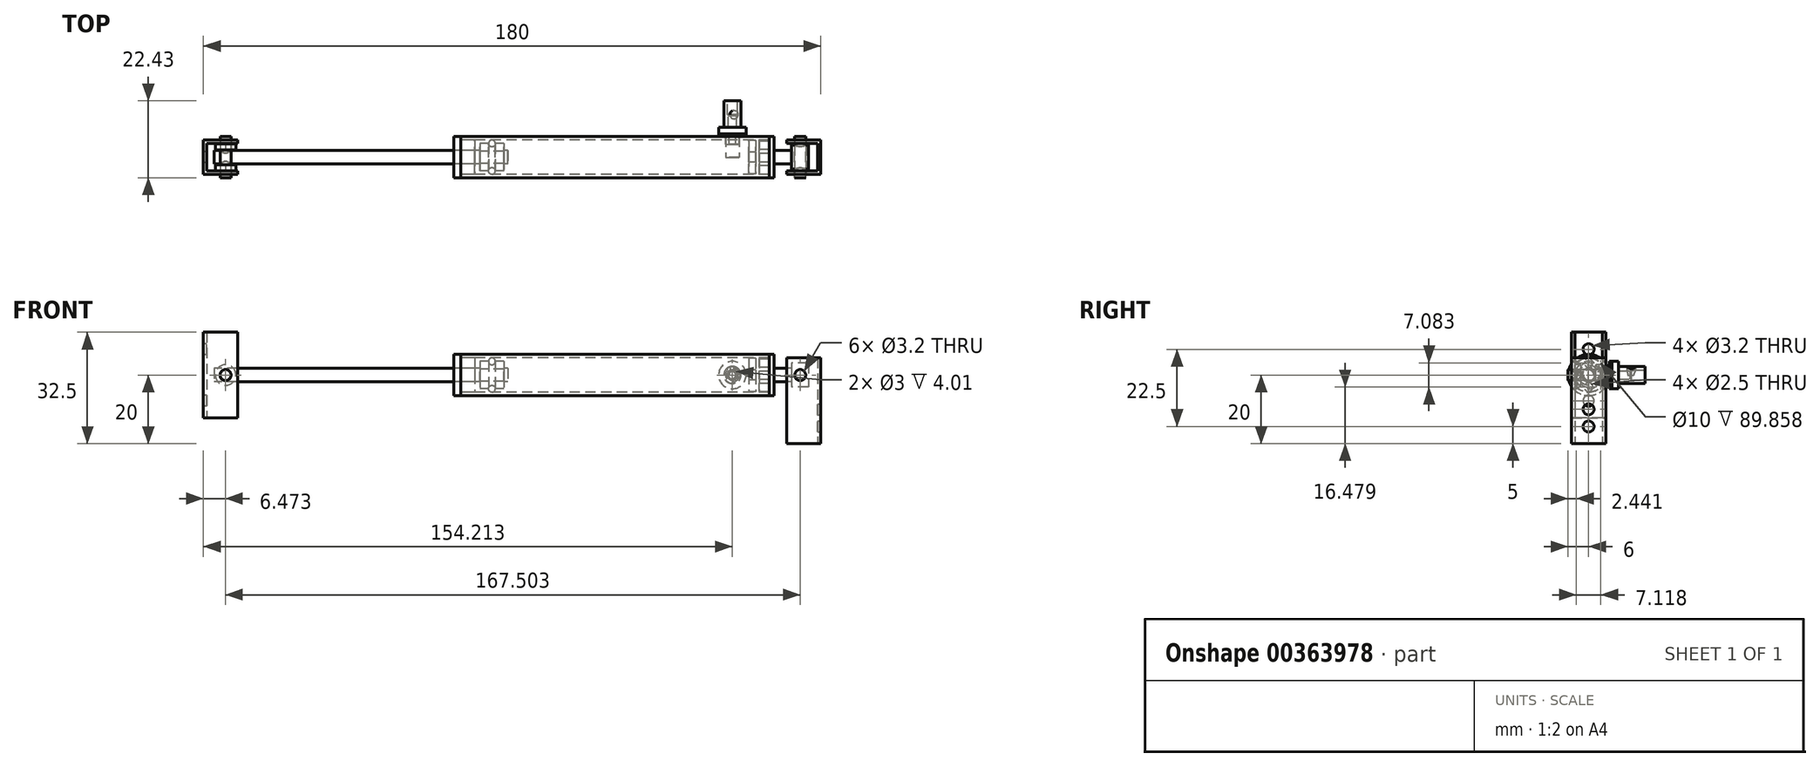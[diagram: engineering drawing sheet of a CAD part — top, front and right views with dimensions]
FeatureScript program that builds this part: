
annotation { "Feature Type Name" : "Feature", "Feature Type Description" : "" }
export const myFeature = defineFeature(function(context is Context, id is Id, definition is map)
    precondition{}
    {
        {
            var Q0;
            Q0=qCreatedBy(makeId("Top.planeOp"),FACE);
            var sketch = newSketch(context, id + "F0", { "sketchPlane" : qUnion([Q0])});
            skLineSegment(sketch, "E0", {"start": v(-90, -5) * mm, "end": v(-90, 5) * mm});
            skLineSegment(sketch, "E1", {"start": v(-90, 5) * mm, "end": v(-80, 5) * mm});
            skLineSegment(sketch, "E2", {"start": v(-80, 5) * mm, "end": v(-80, 4) * mm});
            skLineSegment(sketch, "E3", {"start": v(-80, 4) * mm, "end": v(-89, 4) * mm});
            skLineSegment(sketch, "E4", {"start": v(-89, 4) * mm, "end": v(-89, -4) * mm});
            skLineSegment(sketch, "E5", {"start": v(-89, -4) * mm, "end": v(-80, -4) * mm});
            skLineSegment(sketch, "E6", {"start": v(-80, -4) * mm, "end": v(-80, -5) * mm});
            skLineSegment(sketch, "E7", {"start": v(-80, -5) * mm, "end": v(-90, -5) * mm});
            skLineSegment(sketch, "E8.MirrorCS", {"start": v(80, 5) * mm, "end": v(80, 4) * mm});
            skLineSegment(sketch, "E9.MirrorCS", {"start": v(80, -4) * mm, "end": v(80, -5) * mm});
            skLineSegment(sketch, "E10.MirrorCS", {"start": v(80, 4) * mm, "end": v(89, 4) * mm});
            skLineSegment(sketch, "E11.MirrorCS", {"start": v(90, 5) * mm, "end": v(80, 5) * mm});
            skLineSegment(sketch, "E12.MirrorCS", {"start": v(90, -5) * mm, "end": v(90, 5) * mm});
            skLineSegment(sketch, "E13.MirrorCS", {"start": v(89, -4) * mm, "end": v(80, -4) * mm});
            skLineSegment(sketch, "E14.MirrorCS", {"start": v(80, -5) * mm, "end": v(90, -5) * mm});
            skLineSegment(sketch, "E15.MirrorCS", {"start": v(89, 4) * mm, "end": v(89, -4) * mm});
            skLineSegment(sketch, "E16.bottom", {"start": v(-80, 5) * mm, "end": v(-15, 5) * mm, "construction": true});
            skLineSegment(sketch, "E16.top", {"start": v(-80, -5) * mm, "end": v(-15, -5) * mm, "construction": true});
            skLineSegment(sketch, "E16.left", {"start": v(-80, 5) * mm, "end": v(-80, -5) * mm, "construction": true});
            skLineSegment(sketch, "E16.right", {"start": v(-15, 5) * mm, "end": v(-15, -5) * mm, "construction": true});
            skLineSegment(sketch, "E17.bottom", {"start": v(-86.5, 3.92) * mm, "end": v(-80.5, 3.92) * mm});
            skLineSegment(sketch, "E17.top", {"start": v(-86.5, 2.12) * mm, "end": v(-80.5, 2.12) * mm});
            skLineSegment(sketch, "E17.left", {"start": v(-86.5, 3.92) * mm, "end": v(-86.5, 2.12) * mm});
            skLineSegment(sketch, "E17.right", {"start": v(-80.5, 3.92) * mm, "end": v(-80.5, 2.12) * mm});
            skLineSegment(sketch, "E18", {"start": v(-83.5, 6.91) * mm, "end": v(-83.5, -7.28) * mm, "construction": true});
            skLineSegment(sketch, "E19", {"start": v(-83.5, -7.28) * mm, "end": v(-83.5, 6.04) * mm});
            skLineSegment(sketch, "E20.bottom", {"start": v(-85.1, 2.12) * mm, "end": v(-81.9, 2.12) * mm});
            skLineSegment(sketch, "E20.top", {"start": v(-85.1, 3.92) * mm, "end": v(-81.9, 3.92) * mm});
            skLineSegment(sketch, "E20.left", {"start": v(-85.1, 2.12) * mm, "end": v(-85.1, 3.92) * mm});
            skLineSegment(sketch, "E20.right", {"start": v(-81.9, 2.12) * mm, "end": v(-81.9, 3.92) * mm});
            skLineSegment(sketch, "E21.bottom", {"start": v(-86.5, -2.16) * mm, "end": v(-80.5, -2.16) * mm});
            skLineSegment(sketch, "E21.top", {"start": v(-86.5, -3.96) * mm, "end": v(-80.5, -3.96) * mm});
            skLineSegment(sketch, "E21.left", {"start": v(-86.5, -2.16) * mm, "end": v(-86.5, -3.96) * mm});
            skLineSegment(sketch, "E21.right", {"start": v(-80.5, -2.16) * mm, "end": v(-80.5, -3.96) * mm});
            skPoint(sketch, "E22.startSnap0", {"position": v(-83.5, -2.16) * mm});
            skLineSegment(sketch, "E23.bottom", {"start": v(-85.1, -3.96) * mm, "end": v(-81.9, -3.96) * mm});
            skLineSegment(sketch, "E23.top", {"start": v(-85.1, -2.16) * mm, "end": v(-81.9, -2.16) * mm});
            skLineSegment(sketch, "E23.left", {"start": v(-85.1, -3.96) * mm, "end": v(-85.1, -2.16) * mm});
            skLineSegment(sketch, "E23.right", {"start": v(-81.9, -3.96) * mm, "end": v(-81.9, -2.16) * mm});
            skSolve(sketch);
        }
        {
            var Q0;
            Q0=makeQuery(id+"F0.imprint","IMPRINT",FACE,{"disambiguationData":[TD([[makeQuery(id+"F0.imprint","IMPRINT",EDGE,{"derivedFrom":sQuery(id+"F0.wireOp",EDGE,"E0")}),-1.0]])]});
            var Q1;
            {var subQ5=sQuery(id+"F0.wireOp",EDGE,"E2");Q1=makeQuery(id+"F0.imprint","IMPRINT",FACE,{"disambiguationData":[TD([[makeQuery(id+"F0.imprint","IMPRINT",EDGE,{"derivedFrom":subQ5}),-1.0]])]});}
            var Q2;
            {var subQ0=sQuery(id+"F0.wireOp",EDGE,"E6");Q2=makeQuery(id+"F0.imprint","IMPRINT",FACE,{"disambiguationData":[TD([[makeQuery(id+"F0.imprint","IMPRINT",EDGE,{"derivedFrom":subQ0}),-1.0]])]});}
            extrude(context, id + "F1", {"entities" : qUnion([Q0, Q1, Q2]), "endBound" : BoundingType.SYMMETRIC, "depth" : 25 * mm});
        }
        {
            var Q0;
            Q0=makeQuery(id+"F0.imprint","IMPRINT",FACE,{"disambiguationData":[TD([[makeQuery(id+"F0.imprint","IMPRINT",EDGE,{"derivedFrom":sQuery(id+"F0.wireOp",EDGE,"E8.MirrorCS")}),1.0]])]});
            extrude(context, id + "F2", {"entities" : qUnion([Q0]), "depth" : 5 * mm, "hasSecondDirection" : true, "secondDirectionOppositeDirection" : true, "secondDirectionDepth" : 20 * mm});
        }
        {
            var Q0;
            Q0=qCreatedBy(makeId("Top.planeOp"),FACE);
            var sketch = newSketch(context, id + "F3", { "sketchPlane" : qUnion([Q0])});
            skLineSegment(sketch, "E24.bottom", {"start": v(-14.93, 6) * mm, "end": v(74.93, 6) * mm});
            skLineSegment(sketch, "E24.top", {"start": v(-14.93, -6) * mm, "end": v(74.93, -6) * mm});
            skLineSegment(sketch, "E24.left", {"start": v(-14.93, 6) * mm, "end": v(-14.93, -6) * mm});
            skLineSegment(sketch, "E24.right", {"start": v(74.93, 6) * mm, "end": v(74.93, -6) * mm});
            skLineSegment(sketch, "E25.top", {"start": v(-14.93, 5) * mm, "end": v(74.93, 5) * mm});
            skLineSegment(sketch, "E25.left", {"start": v(-14.93, 6) * mm, "end": v(-14.93, 5) * mm});
            skLineSegment(sketch, "E25.right", {"start": v(74.93, 6) * mm, "end": v(74.93, 5) * mm});
            skLineSegment(sketch, "E26.top", {"start": v(-14.93, -5) * mm, "end": v(74.93, -5) * mm});
            skLineSegment(sketch, "E26.left", {"start": v(-14.93, -6) * mm, "end": v(-14.93, -5) * mm});
            skLineSegment(sketch, "E26.right", {"start": v(74.93, -6) * mm, "end": v(74.93, -5) * mm});
            skLineSegment(sketch, "E27", {"start": v(-95.99, 0) * mm, "end": v(102.37, 0) * mm, "construction": true});
            skPoint(sketch, "E27.endSnap0", {"position": v(-14.93, 0) * mm});
            skSolve(sketch);
        }
        {
            var Q0;
            Q0=qCreatedBy(makeId("Top.planeOp"),FACE);
            var sketch = newSketch(context, id + "F4", { "sketchPlane" : qUnion([Q0])});
            skLineSegment(sketch, "E28.bottom", {"start": v(-108.9, 0) * mm, "end": v(81.37, 0) * mm, "construction": true});
            skLineSegment(sketch, "E28.top", {"start": v(-108.9, 0) * mm, "end": v(81.37, 0) * mm});
            skLineSegment(sketch, "E28.left", {"start": v(-108.9, 0) * mm, "end": v(-108.9, 0) * mm});
            skLineSegment(sketch, "E28.right", {"start": v(81.37, 0) * mm, "end": v(81.37, 0) * mm});
            skLineSegment(sketch, "E29.bottom", {"start": v(-86.9, 2) * mm, "end": v(-1.24, 2) * mm});
            skLineSegment(sketch, "E29.top", {"start": v(-86.9, -2) * mm, "end": v(-1.24, -2) * mm});
            skLineSegment(sketch, "E29.left", {"start": v(-86.9, 2) * mm, "end": v(-86.9, -2) * mm});
            skLineSegment(sketch, "E29.right", {"start": v(-1.24, 2) * mm, "end": v(-1.24, -2) * mm});
            skSolve(sketch);
        }
        {
            var Q0;
            Q0=makeQuery(id+"F3.imprint","IMPRINT",FACE,{"disambiguationData":[TD([[makeQuery(id+"F3.imprint","IMPRINT",EDGE,{"derivedFrom":sQuery(id+"F3.wireOp",EDGE,"E24.bottom")}),-1.0]])]});
            var Q1;
            Q1=sQuery(id+"F3.wireOp",EDGE,"E27");
            revolve(context, id + "F5", {"entities" : qUnion([Q0]), "axis" : qUnion([Q1]), "revolveType" : RevolveType.FULL});
        }
        {
            var Q0;
            {var subQ5=sQuery(id+"F4.wireOp",EDGE,"E29.bottom");Q0=makeQuery(id+"F4.imprint","IMPRINT",FACE,{"disambiguationData":[TD([[makeQuery(id+"F4.imprint","IMPRINT",EDGE,{"derivedFrom":subQ5}),-1.0]])]});}
            var Q1;
            Q1=sQuery(id+"F4.wireOp",EDGE,"E28.top");
            revolve(context, id + "F6", {"entities" : qUnion([Q0]), "axis" : qUnion([Q1]), "revolveType" : RevolveType.FULL});
        }
        {
            var Q0;
            Q0=qCreatedBy(makeId("Top.planeOp"),FACE);
            var sketch = newSketch(context, id + "F7", { "sketchPlane" : qUnion([Q0])});
            skLineSegment(sketch, "E30.bottom", {"start": v(-9.38, 4) * mm, "end": v(-6.88, 4) * mm});
            skLineSegment(sketch, "E30.top", {"start": v(-9.38, -4) * mm, "end": v(-2.38, -4) * mm});
            skLineSegment(sketch, "E30.left", {"start": v(-9.38, 4) * mm, "end": v(-9.38, -4) * mm});
            skLineSegment(sketch, "E30.right", {"start": v(-2.38, 4) * mm, "end": v(-2.38, -4) * mm});
            skCircle(sketch, "E31", {"center": v(-5.88, 4) * mm, "radius": 1 * mm});
            skLineSegment(sketch, "E32.top", {"start": v(-9.38, 1.77) * mm, "end": v(-2.38, 1.77) * mm});
            skLineSegment(sketch, "E32.left", {"start": v(-9.38, 4) * mm, "end": v(-9.38, 1.77) * mm});
            skLineSegment(sketch, "E32.right", {"start": v(-2.38, 4) * mm, "end": v(-2.38, 1.77) * mm});
            skLineSegment(sketch, "E33", {"start": v(-4.88, 4) * mm, "end": v(-2.38, 4) * mm});
            skLineSegment(sketch, "E34", {"start": v(-7.97, 0) * mm, "end": v(19.48, 0) * mm, "construction": true});
            skLineSegment(sketch, "E35.bottom", {"start": v(-5.83, 14.1) * mm, "end": v(54.17, 14.1) * mm, "construction": true});
            skLineSegment(sketch, "E35.top", {"start": v(-5.83, -9.63) * mm, "end": v(54.17, -9.63) * mm, "construction": true});
            skLineSegment(sketch, "E35.left", {"start": v(-5.83, 14.1) * mm, "end": v(-5.83, -9.63) * mm, "construction": true});
            skLineSegment(sketch, "E35.right", {"start": v(54.17, 14.1) * mm, "end": v(54.17, -9.63) * mm, "construction": true});
            skSolve(sketch);
        }
        {
            var Q0;
            {var subQ0=sQuery(id+"F7.wireOp",EDGE,"E31");var subQ1=makeQuery(id+"F7.imprint","INTERSECT",VERTEX,{"derivedFrom":[subQ0,sQuery(id+"F7.wireOp",EDGE,"E30.bottom")]});Q0=makeQuery(id+"F7.imprint","IMPRINT",FACE,{"disambiguationData":[TD([[makeQuery(id+"F7.imprint","IMPRINT",EDGE,{"disambiguationData":[TD([[subQ1,1.0]])],"derivedFrom":subQ0}),1.0]])]});}
            var Q1;
            Q1=sQuery(id+"F7.wireOp",EDGE,"E34");
            revolve(context, id + "F8", {"entities" : qUnion([Q0]), "axis" : qUnion([Q1]), "revolveType" : RevolveType.FULL});
        }
        {
            var Q0;
            {var subQ0=sQuery(id+"F7.wireOp",EDGE,"E30.bottom");Q0=makeQuery(id+"F7.imprint","IMPRINT",FACE,{"disambiguationData":[TD([[makeQuery(id+"F7.imprint","IMPRINT",EDGE,{"derivedFrom":subQ0}),-1.0]])]});}
            var Q1;
            Q1=sQuery(id+"F7.wireOp",EDGE,"E34");
            revolve(context, id + "F9", {"operationType" : NewBodyOperationType.REMOVE, "entities" : qUnion([Q0]), "axis" : qUnion([Q1]), "revolveType" : RevolveType.FULL});
        }
        {
            var Q0;
            {var subQ0=sQuery(id+"F7.wireOp",EDGE,"E30.bottom");Q0=makeQuery(id+"F7.imprint","IMPRINT",FACE,{"disambiguationData":[TD([[makeQuery(id+"F7.imprint","IMPRINT",EDGE,{"derivedFrom":subQ0}),-1.0]])]});}
            var Q1;
            Q1=sQuery(id+"F7.wireOp",EDGE,"E34");
            revolve(context, id + "F10", {"entities" : qUnion([Q0]), "axis" : qUnion([Q1]), "revolveType" : RevolveType.FULL});
        }
        {
            var Q0;
            {var subQ0=sQuery(id+"F7.wireOp",EDGE,"E31");var subQ1=makeQuery(id+"F7.imprint","INTERSECT",VERTEX,{"derivedFrom":[subQ0,sQuery(id+"F7.wireOp",EDGE,"E30.bottom")]});Q0=makeQuery(id+"F7.imprint","IMPRINT",FACE,{"disambiguationData":[TD([[makeQuery(id+"F7.imprint","IMPRINT",EDGE,{"disambiguationData":[TD([[subQ1,1.0]])],"derivedFrom":subQ0}),1.0]])]});}
            var Q1;
            Q1=sQuery(id+"F7.wireOp",EDGE,"E31");
            var Q2;
            Q2=sQuery(id+"F7.wireOp",EDGE,"E34");
            revolve(context, id + "F11", {"entities" : qUnion([Q0]), "surfaceEntities" : qUnion([Q1]), "axis" : qUnion([Q2]), "revolveType" : RevolveType.FULL});
        }
        {
            var Q0;
            Q0=makeQuery(id+"F8.opRevolve","SWEPT_BODY",BODY,{"disambiguationData":[OSD([sQuery(id+"F7.wireOp",EDGE,"E31")])]});
            deleteBodies(context, id + "F12", {"entities" : qUnion([Q0])});
        }
        {
            var Q0;
            Q0=qCreatedBy(makeId("Top.planeOp"),FACE);
            var sketch = newSketch(context, id + "F13", { "sketchPlane" : qUnion([Q0])});
            skLineSegment(sketch, "E36.bottom", {"start": v(-14.94, 6) * mm, "end": v(-16.94, 6) * mm});
            skLineSegment(sketch, "E36.top", {"start": v(-14.94, -6) * mm, "end": v(-16.94, -6) * mm});
            skLineSegment(sketch, "E36.left", {"start": v(-14.94, 6) * mm, "end": v(-14.94, -6) * mm});
            skLineSegment(sketch, "E36.right", {"start": v(-16.94, 6) * mm, "end": v(-16.94, -6) * mm});
            skLineSegment(sketch, "E37.bottom", {"start": v(-14.94, 5) * mm, "end": v(-10.94, 5) * mm});
            skLineSegment(sketch, "E37.top", {"start": v(-14.94, -5) * mm, "end": v(-10.94, -5) * mm});
            skLineSegment(sketch, "E37.left", {"start": v(-14.94, 5) * mm, "end": v(-14.94, -5) * mm});
            skLineSegment(sketch, "E37.right", {"start": v(-10.94, 5) * mm, "end": v(-10.94, -5) * mm});
            skLineSegment(sketch, "E38", {"start": v(-16.94, 2) * mm, "end": v(-10.94, 2) * mm});
            skLineSegment(sketch, "E39", {"start": v(-16.94, -1.98) * mm, "end": v(-10.94, -1.98) * mm});
            skSolve(sketch);
        }
        {
            var Q0;
            {var subQ6=sQuery(id+"F13.wireOp",EDGE,"E36.bottom");Q0=makeQuery(id+"F13.imprint","IMPRINT",FACE,{"disambiguationData":[TD([[makeQuery(id+"F13.imprint","IMPRINT",EDGE,{"derivedFrom":subQ6}),1.0]])]});}
            var Q1;
            {var subQ0=sQuery(id+"F13.wireOp",EDGE,"E37.bottom");Q1=makeQuery(id+"F13.imprint","IMPRINT",FACE,{"disambiguationData":[TD([[makeQuery(id+"F13.imprint","IMPRINT",EDGE,{"derivedFrom":subQ0}),-1.0]])]});}
            var Q2;
            Q2=sQuery(id+"F4.wireOp",EDGE,"E28.top");
            revolve(context, id + "F14", {"entities" : qUnion([Q0, Q1]), "axis" : qUnion([Q2]), "revolveType" : RevolveType.FULL});
        }
        {
            var Q0;
            Q0=qCreatedBy(makeId("Top.planeOp"),FACE);
            var sketch = newSketch(context, id + "F15", { "sketchPlane" : qUnion([Q0])});
            skLineSegment(sketch, "E40.bottom", {"start": v(74.9, 6) * mm, "end": v(76.3, 6) * mm});
            skLineSegment(sketch, "E40.top", {"start": v(74.9, -6) * mm, "end": v(76.3, -6) * mm});
            skLineSegment(sketch, "E40.left", {"start": v(74.9, 6) * mm, "end": v(74.9, -6) * mm});
            skLineSegment(sketch, "E40.right", {"start": v(76.3, 6) * mm, "end": v(76.3, -6) * mm});
            skLineSegment(sketch, "E41.bottom", {"start": v(74.9, 5) * mm, "end": v(72.07, 5) * mm});
            skLineSegment(sketch, "E41.top", {"start": v(74.9, -5) * mm, "end": v(72.07, -5) * mm});
            skLineSegment(sketch, "E41.left", {"start": v(74.9, 5) * mm, "end": v(74.9, -5) * mm});
            skLineSegment(sketch, "E41.right", {"start": v(72.07, 5) * mm, "end": v(72.07, -5) * mm});
            skLineSegment(sketch, "E42.bottom", {"start": v(76.3, 2) * mm, "end": v(81.44, 2) * mm});
            skLineSegment(sketch, "E42.top", {"start": v(76.3, -2) * mm, "end": v(81.44, -2) * mm});
            skLineSegment(sketch, "E42.left", {"start": v(76.3, 2) * mm, "end": v(76.3, -2) * mm});
            skLineSegment(sketch, "E42.right", {"start": v(81.44, 2) * mm, "end": v(81.44, -2) * mm});
            skLineSegment(sketch, "E43.bottom", {"start": v(81.44, 3.5) * mm, "end": v(86.39, 3.5) * mm});
            skLineSegment(sketch, "E43.top", {"start": v(81.44, -3.5) * mm, "end": v(86.39, -3.5) * mm});
            skLineSegment(sketch, "E43.left", {"start": v(81.44, 3.5) * mm, "end": v(81.44, -3.5) * mm});
            skLineSegment(sketch, "E43.right", {"start": v(86.39, 3.5) * mm, "end": v(86.39, -3.5) * mm});
            skLineSegment(sketch, "E44", {"start": v(66.23, 0) * mm, "end": v(91.9, 0) * mm, "construction": true});
            skPoint(sketch, "E44.endSnap0", {"position": v(81.44, 0) * mm});
            skLineSegment(sketch, "E45", {"start": v(72.07, 0) * mm, "end": v(86.39, 0) * mm});
            skLineSegment(sketch, "E46.bottom", {"start": v(69, 4.9) * mm, "end": v(71, 4.9) * mm});
            skLineSegment(sketch, "E46.top", {"start": v(69, 1.5) * mm, "end": v(71, 1.5) * mm});
            skLineSegment(sketch, "E46.left", {"start": v(69, 4.9) * mm, "end": v(69, 1.5) * mm});
            skLineSegment(sketch, "E46.right", {"start": v(71, 4.9) * mm, "end": v(71, 1.5) * mm});
            skSolve(sketch);
        }
        {
            var Q0;
            Q0=makeQuery(id+"F15.imprint","IMPRINT",FACE,{"disambiguationData":[TD([[makeQuery(id+"F15.imprint","IMPRINT",EDGE,{"derivedFrom":sQuery(id+"F15.wireOp",EDGE,"E41.bottom")}),1.0]])]});
            var Q1;
            {var subQ3=sQuery(id+"F15.wireOp",EDGE,"E40.bottom");Q1=makeQuery(id+"F15.imprint","IMPRINT",FACE,{"disambiguationData":[TD([[makeQuery(id+"F15.imprint","IMPRINT",EDGE,{"derivedFrom":subQ3}),-1.0]])]});}
            var Q2;
            {var subQ0=sQuery(id+"F15.wireOp",EDGE,"E42.bottom");Q2=makeQuery(id+"F15.imprint","IMPRINT",FACE,{"disambiguationData":[TD([[makeQuery(id+"F15.imprint","IMPRINT",EDGE,{"derivedFrom":subQ0}),-1.0]])]});}
            var Q3;
            {var subQ3=sQuery(id+"F15.wireOp",EDGE,"E43.bottom");Q3=makeQuery(id+"F15.imprint","IMPRINT",FACE,{"disambiguationData":[TD([[makeQuery(id+"F15.imprint","IMPRINT",EDGE,{"derivedFrom":subQ3}),-1.0]])]});}
            var Q4;
            Q4=sQuery(id+"F4.wireOp",EDGE,"E28.top");
            revolve(context, id + "F16", {"entities" : qUnion([Q0, Q1, Q2, Q3]), "axis" : qUnion([Q4]), "revolveType" : RevolveType.FULL});
        }
        {
            var Q0;
            Q0=makeQuery(id+"F16.opRevolve","SWEPT_FACE",FACE,{"disambiguationData":[OSD([sQuery(id+"F15.wireOp",EDGE,"E40.right")])]});
            var sketch = newSketch(context, id + "F17", { "sketchPlane" : qUnion([Q0])});
            skCircle(sketch, "E47", {"center": v(-0.02, 3.56) * mm, "radius": 1.25 * mm});
            skCircle(sketch, "E48", {"center": v(0, 0) * mm, "radius": 3.56 * mm, "construction": true});
            skCircle(sketch, "E49", {"center": v(3.56, 0) * mm, "radius": 1.25 * mm});
            skCircle(sketch, "E50", {"center": v(-0.02, -3.52) * mm, "radius": 1.25 * mm});
            skCircle(sketch, "E51", {"center": v(-3.56, 0) * mm, "radius": 1.25 * mm});
            skSolve(sketch);
        }
        {
            var Q0;
            Q0=makeQuery(id+"F17.imprint","IMPRINT",FACE,{"disambiguationData":[TD([[makeQuery(id+"F17.imprint","IMPRINT",EDGE,{"derivedFrom":sQuery(id+"F17.wireOp",EDGE,"E47")}),1.0]])]});
            var Q1;
            Q1=makeQuery(id+"F17.imprint","IMPRINT",FACE,{"disambiguationData":[TD([[makeQuery(id+"F17.imprint","IMPRINT",EDGE,{"derivedFrom":sQuery(id+"F17.wireOp",EDGE,"E51")}),1.0]])]});
            var Q2;
            Q2=makeQuery(id+"F17.imprint","IMPRINT",FACE,{"disambiguationData":[TD([[makeQuery(id+"F17.imprint","IMPRINT",EDGE,{"derivedFrom":sQuery(id+"F17.wireOp",EDGE,"E50")}),1.0]])]});
            var Q3;
            Q3=makeQuery(id+"F17.imprint","IMPRINT",FACE,{"disambiguationData":[TD([[makeQuery(id+"F17.imprint","IMPRINT",EDGE,{"derivedFrom":sQuery(id+"F17.wireOp",EDGE,"E49")}),1.0]])]});
            extrude(context, id + "F18", {"entities" : qUnion([Q0, Q1, Q2, Q3]), "operationType" : NewBodyOperationType.REMOVE, "endBound" : BoundingType.UP_TO_NEXT, "oppositeDirection" : true, "depth" : 25 * mm});
        }
        {
            var Q0;
            Q0=makeQuery(id+"F15.imprint","IMPRINT",FACE,{"disambiguationData":[TD([[makeQuery(id+"F15.imprint","IMPRINT",EDGE,{"derivedFrom":sQuery(id+"F15.wireOp",EDGE,"E46.bottom")}),-1.0]])]});
            var Q1;
            Q1=sQuery(id+"F4.wireOp",EDGE,"E28.top");
            revolve(context, id + "F19", {"entities" : qUnion([Q0]), "axis" : qUnion([Q1]), "revolveType" : RevolveType.FULL});
        }
        {
            var Q0;
            {var subQ0=sQuery(id+"F0.wireOp",EDGE,"E17.right");Q0=makeQuery(id+"F0.imprint","IMPRINT",FACE,{"disambiguationData":[TD([[makeQuery(id+"F0.imprint","IMPRINT",EDGE,{"derivedFrom":subQ0}),-1.0]])]});}
            var Q1;
            {var subQ0=sQuery(id+"F0.wireOp",EDGE,"E21.right");Q1=makeQuery(id+"F0.imprint","IMPRINT",FACE,{"disambiguationData":[TD([[makeQuery(id+"F0.imprint","IMPRINT",EDGE,{"derivedFrom":subQ0}),-1.0]])]});}
            var Q2;
            Q2=sQuery(id+"F0.wireOp",EDGE,"E19");
            revolve(context, id + "F20", {"operationType" : NewBodyOperationType.ADD, "entities" : qUnion([Q0, Q1]), "axis" : qUnion([Q2]), "revolveType" : RevolveType.FULL});
        }
        {
            var Q0;
            Q0=makeQuery(id+"F1.opExtrude","SWEPT_FACE",FACE,{"disambiguationData":[OSD([sQuery(id+"F0.wireOp",EDGE,"E7")])]});
            var sketch = newSketch(context, id + "F21", { "sketchPlane" : qUnion([Q0])});
            skCircle(sketch, "E52", {"center": v(-83.53, 0) * mm, "radius": 1.6 * mm});
            skSolve(sketch);
        }
        {
            var Q0;
            Q0=makeQuery(id+"F21.imprint","IMPRINT",FACE,{"disambiguationData":[TD([[makeQuery(id+"F21.imprint","IMPRINT",EDGE,{"derivedFrom":sQuery(id+"F21.wireOp",EDGE,"E52")}),1.0]])]});
            extrude(context, id + "F22", {"entities" : qUnion([Q0]), "oppositeDirection" : true, "depth" : 12 * mm, "hasSecondDirection" : true, "secondDirectionOppositeDirection" : true, "secondDirectionDepth" : -2 * mm});
        }
        {
            var Q0;
            Q0=qCreatedBy(makeId("Top.planeOp"),FACE);
            var sketch = newSketch(context, id + "F23", { "sketchPlane" : qUnion([Q0])});
            skLineSegment(sketch, "E53.bottom", {"start": v(60.21, 6.76) * mm, "end": v(68.21, 6.76) * mm});
            skLineSegment(sketch, "E53.top", {"start": v(60.21, 8.76) * mm, "end": v(68.21, 8.76) * mm});
            skLineSegment(sketch, "E53.left", {"start": v(60.21, 6.76) * mm, "end": v(60.21, 8.76) * mm});
            skLineSegment(sketch, "E53.right", {"start": v(68.21, 6.76) * mm, "end": v(68.21, 8.76) * mm});
            skLineSegment(sketch, "E54.bottom", {"start": v(63.21, 8.76) * mm, "end": v(65.21, 8.76) * mm});
            skLineSegment(sketch, "E54.top", {"start": v(63.21, 6.76) * mm, "end": v(65.21, 6.76) * mm});
            skLineSegment(sketch, "E54.left", {"start": v(63.21, 8.76) * mm, "end": v(63.21, 3.79) * mm});
            skLineSegment(sketch, "E54.right", {"start": v(65.21, 8.76) * mm, "end": v(65.21, 3.79) * mm});
            skLineSegment(sketch, "E55", {"start": v(64.21, 25.99) * mm, "end": v(64.21, 1.15) * mm, "construction": true});
            skLineSegment(sketch, "E56.bottom", {"start": v(62.21, 6.76) * mm, "end": v(66.21, 6.76) * mm});
            skLineSegment(sketch, "E56.top", {"start": v(62.21, 3.79) * mm, "end": v(66.21, 3.79) * mm});
            skLineSegment(sketch, "E56.left", {"start": v(62.21, 6.76) * mm, "end": v(62.21, 3.79) * mm});
            skLineSegment(sketch, "E56.right", {"start": v(66.21, 6.76) * mm, "end": v(66.21, 3.79) * mm});
            skLineSegment(sketch, "E57.bottom", {"start": v(60.21, 6.67) * mm, "end": v(61.81, 6.67) * mm});
            skLineSegment(sketch, "E57.top", {"start": v(60.21, 6.08) * mm, "end": v(61.81, 6.08) * mm});
            skLineSegment(sketch, "E57.left", {"start": v(60.21, 6.67) * mm, "end": v(60.21, 6.08) * mm});
            skLineSegment(sketch, "E57.right", {"start": v(61.81, 6.67) * mm, "end": v(61.81, 6.08) * mm});
            skLineSegment(sketch, "E58.bottom", {"start": v(61.71, 8.76) * mm, "end": v(66.71, 8.76) * mm});
            skLineSegment(sketch, "E58.top", {"start": v(61.71, 16.43) * mm, "end": v(66.71, 16.43) * mm});
            skLineSegment(sketch, "E58.left", {"start": v(61.71, 8.76) * mm, "end": v(61.71, 16.43) * mm});
            skLineSegment(sketch, "E58.right", {"start": v(66.71, 8.76) * mm, "end": v(66.71, 16.43) * mm});
            skLineSegment(sketch, "E59.bottom", {"start": v(63.01, 8.76) * mm, "end": v(65.41, 8.76) * mm});
            skLineSegment(sketch, "E59.top", {"start": v(63.01, 16.43) * mm, "end": v(65.41, 16.43) * mm});
            skLineSegment(sketch, "E59.left", {"start": v(63.01, 8.76) * mm, "end": v(63.01, 16.43) * mm});
            skLineSegment(sketch, "E59.right", {"start": v(65.41, 8.76) * mm, "end": v(65.41, 16.43) * mm});
            skLineSegment(sketch, "E60.bottom", {"start": v(61.46, 20.92) * mm, "end": v(66.96, 20.92) * mm});
            skLineSegment(sketch, "E60.top", {"start": v(61.46, 18.42) * mm, "end": v(66.96, 18.42) * mm});
            skLineSegment(sketch, "E60.left", {"start": v(61.46, 20.92) * mm, "end": v(61.46, 18.42) * mm});
            skLineSegment(sketch, "E60.right", {"start": v(66.96, 20.92) * mm, "end": v(66.96, 18.42) * mm});
            skLineSegment(sketch, "E61.bottom", {"start": v(62.71, 18.42) * mm, "end": v(65.71, 18.42) * mm});
            skLineSegment(sketch, "E61.top", {"start": v(62.71, 12.42) * mm, "end": v(65.71, 12.42) * mm});
            skLineSegment(sketch, "E61.left", {"start": v(62.71, 18.42) * mm, "end": v(62.71, 12.42) * mm});
            skLineSegment(sketch, "E61.right", {"start": v(65.71, 18.42) * mm, "end": v(65.71, 12.42) * mm});
            skCircle(sketch, "E62", {"center": v(64.21, 12.44) * mm, "radius": 1.25 * mm});
            skLineSegment(sketch, "E63.bottom", {"start": v(61.46, 20.92) * mm, "end": v(64.21, 20.92) * mm});
            skLineSegment(sketch, "E63.top", {"start": v(61.46, 18.42) * mm, "end": v(64.21, 18.42) * mm});
            skLineSegment(sketch, "E63.right", {"start": v(64.21, 20.92) * mm, "end": v(64.21, 18.42) * mm});
            skLineSegment(sketch, "E64.bottom", {"start": v(62.71, 18.42) * mm, "end": v(64.21, 18.42) * mm});
            skLineSegment(sketch, "E64.top", {"start": v(62.71, 12.42) * mm, "end": v(64.21, 12.42) * mm});
            skLineSegment(sketch, "E64.right", {"start": v(64.21, 18.42) * mm, "end": v(64.21, 12.42) * mm});
            skSolve(sketch);
        }
        {
            var Q0;
            {var subQ0=sQuery(id+"F23.wireOp",EDGE,"E53.left");Q0=makeQuery(id+"F23.imprint","IMPRINT",FACE,{"disambiguationData":[TD([[makeQuery(id+"F23.imprint","IMPRINT",EDGE,{"derivedFrom":subQ0}),-1.0]])]});}
            var Q1;
            {var subQ5=sQuery(id+"F23.wireOp",EDGE,"E56.left");Q1=makeQuery(id+"F23.imprint","IMPRINT",FACE,{"disambiguationData":[TD([[makeQuery(id+"F23.imprint","IMPRINT",EDGE,{"derivedFrom":subQ5}),1.0]])]});}
            var Q2;
            {var subQ0=sQuery(id+"F23.wireOp",EDGE,"E58.left");Q2=makeQuery(id+"F23.imprint","IMPRINT",FACE,{"disambiguationData":[TD([[makeQuery(id+"F23.imprint","IMPRINT",EDGE,{"derivedFrom":subQ0}),-1.0]])]});}
            var Q3;
            Q3=sQuery(id+"F23.wireOp",EDGE,"E55");
            revolve(context, id + "F24", {"entities" : qUnion([Q0, Q1, Q2]), "axis" : qUnion([Q3]), "revolveType" : RevolveType.FULL});
        }
        {
            var Q0;
            Q0=makeQuery(id+"F23.imprint","IMPRINT",FACE,{"disambiguationData":[TD([[makeQuery(id+"F23.imprint","IMPRINT",EDGE,{"derivedFrom":sQuery(id+"F23.wireOp",EDGE,"E57.bottom")}),-1.0]])]});
            var Q1;
            Q1=sQuery(id+"F23.wireOp",EDGE,"E55");
            revolve(context, id + "F25", {"entities" : qUnion([Q0]), "axis" : qUnion([Q1]), "revolveType" : RevolveType.FULL});
        }
        {
            var Q0;
            Q0=qCreatedBy(makeId("Top.planeOp"),FACE);
            var sketch = newSketch(context, id + "F26", { "sketchPlane" : qUnion([Q0])});
            skCircle(sketch, "E65", {"center": v(64.71, 12.42) * mm, "radius": 1.23 * mm});
            skSolve(sketch);
        }
        {
            var Q0;
            Q0 = qSketchRegion(id + "F26", true);
            extrude(context, id + "F27", {"entities" : qUnion([Q0]), "operationType" : NewBodyOperationType.REMOVE, "endBound" : BoundingType.THROUGH_ALL, "depth" : 25 * mm});
        }
        {
            var Q0;
            Q0=makeQuery(id+"F23.imprint","IMPRINT",FACE,{"disambiguationData":[TD([[makeQuery(id+"F23.imprint","IMPRINT",EDGE,{"derivedFrom":sQuery(id+"F23.wireOp",EDGE,"E63.bottom")}),-1.0]])]});
            var Q1;
            {var subQ1=sQuery(id+"F23.wireOp",EDGE,"E64.bottom");Q1=makeQuery(id+"F23.imprint","IMPRINT",FACE,{"disambiguationData":[TD([[makeQuery(id+"F23.imprint","IMPRINT",EDGE,{"derivedFrom":subQ1}),-1.0]])]});}
            var Q2;
            {var subQ0=sQuery(id+"F23.wireOp",EDGE,"E59.left");var subQ5=sQuery(id+"F23.wireOp",EDGE,"E62");var subQ6=makeQuery(id+"F23.imprint","INTERSECT",VERTEX,{"disambiguationData":[OD(1.0)],"derivedFrom":[subQ0,subQ5]});Q2=makeQuery(id+"F23.imprint","IMPRINT",FACE,{"disambiguationData":[TD([[makeQuery(id+"F23.imprint","IMPRINT",EDGE,{"disambiguationData":[TD([[subQ6,1.0]])],"derivedFrom":subQ5}),-1.0]])]});}
            var Q3;
            Q3=sQuery(id+"F23.wireOp",EDGE,"E55");
            revolve(context, id + "F28", {"entities" : qUnion([Q0, Q1, Q2]), "axis" : qUnion([Q3]), "revolveType" : RevolveType.FULL});
        }
        {
            var Q0;
            Q0=makeQuery(id+"F2.opExtrude","SWEPT_FACE",FACE,{"disambiguationData":[OSD([sQuery(id+"F0.wireOp",EDGE,"E14.MirrorCS")])]});
            var sketch = newSketch(context, id + "F29", { "sketchPlane" : qUnion([Q0])});
            skCircle(sketch, "E66", {"center": v(83.98, 0) * mm, "radius": 1.6 * mm});
            skSolve(sketch);
        }
        {
            var Q0;
            Q0=makeQuery(id+"F29.imprint","IMPRINT",FACE,{"disambiguationData":[TD([[makeQuery(id+"F29.imprint","IMPRINT",EDGE,{"derivedFrom":sQuery(id+"F29.wireOp",EDGE,"E66")}),1.0]])]});
            var Q1;
            Q1=sQuery(id+"F29.wireOp",EDGE,"E66");
            extrude(context, id + "F30", {"entities" : qUnion([Q0]), "surfaceEntities" : qUnion([Q1]), "oppositeDirection" : true, "depth" : 12 * mm, "hasSecondDirection" : true, "secondDirectionOppositeDirection" : true, "secondDirectionDepth" : -2 * mm});
        }
        {
            var Q0;
            Q0=qCreatedBy(makeId("Front.planeOp"),FACE);
            var sketch = newSketch(context, id + "F31", { "sketchPlane" : qUnion([Q0])});
            skCircle(sketch, "E67", {"center": v(-83.53, 0) * mm, "radius": 1.6 * mm});
            skCircle(sketch, "E68", {"center": v(83.98, 0) * mm, "radius": 1.6 * mm});
            skSolve(sketch);
        }
        {
            var Q0;
            Q0 = qSketchRegion(id + "F31", true);
            var Q1;
            Q1=sQuery(id+"F31.wireOp",EDGE,"E68");
            extrude(context, id + "F32", {"entities" : qUnion([Q0]), "operationType" : NewBodyOperationType.REMOVE, "surfaceEntities" : qUnion([Q1]), "endBound" : BoundingType.SYMMETRIC, "oppositeDirection" : true, "depth" : 25 * mm});
        }
        {
            var Q0;
            Q0 = qSketchRegion(id + "F31", true);
            var Q1;
            Q1=sQuery(id+"F31.wireOp",EDGE,"E67");
            extrude(context, id + "F33", {"entities" : qUnion([Q0]), "operationType" : NewBodyOperationType.REMOVE, "surfaceEntities" : qUnion([Q1]), "endBound" : BoundingType.SYMMETRIC, "oppositeDirection" : true, "depth" : 25 * mm});
        }
        {
            var Q0;
            Q0=makeQuery(id+"F31.imprint","IMPRINT",FACE,{"disambiguationData":[TD([[makeQuery(id+"F31.imprint","IMPRINT",EDGE,{"derivedFrom":sQuery(id+"F31.wireOp",EDGE,"E67")}),1.0]])]});
            var Q1;
            Q1=sQuery(id+"F31.wireOp",EDGE,"E67");
            extrude(context, id + "F34", {"entities" : qUnion([Q0]), "surfaceEntities" : qUnion([Q1]), "depth" : 6 * mm, "hasSecondDirection" : true, "secondDirectionOppositeDirection" : true, "secondDirectionDepth" : 6 * mm});
        }
        {
            var Q0;
            Q0=makeQuery(id+"F31.imprint","IMPRINT",FACE,{"disambiguationData":[TD([[makeQuery(id+"F31.imprint","IMPRINT",EDGE,{"derivedFrom":sQuery(id+"F31.wireOp",EDGE,"E68")}),1.0]])]});
            var Q1;
            Q1=sQuery(id+"F31.wireOp",EDGE,"E68");
            extrude(context, id + "F35", {"entities" : qUnion([Q0]), "surfaceEntities" : qUnion([Q1]), "depth" : 6 * mm, "hasSecondDirection" : true, "secondDirectionOppositeDirection" : true, "secondDirectionDepth" : 6 * mm});
        }
        {
            var Q0;
            Q0=qCreatedBy(makeId("Front.planeOp"),FACE);
            var sketch = newSketch(context, id + "F36", { "sketchPlane" : qUnion([Q0])});
            skCircle(sketch, "E69", {"center": v(64.21, 0) * mm, "radius": 2 * mm});
            skSolve(sketch);
        }
        {
            var Q0;
            Q0=makeQuery(id+"F36.imprint","IMPRINT",FACE,{"disambiguationData":[TD([[makeQuery(id+"F36.imprint","IMPRINT",EDGE,{"derivedFrom":sQuery(id+"F36.wireOp",EDGE,"E69")}),1.0]])]});
            var Q1;
            Q1=sQuery(id+"F36.wireOp",EDGE,"E69");
            extrude(context, id + "F37", {"entities" : qUnion([Q0]), "surfaceEntities" : qUnion([Q1]), "oppositeDirection" : true, "depth" : 6 * mm});
        }
        {
            var Q0;
            Q0=makeQuery(id+"F2.opExtrude","SWEPT_FACE",FACE,{"disambiguationData":[OSD([sQuery(id+"F0.wireOp",EDGE,"E12.MirrorCS")])]});
            var sketch = newSketch(context, id + "F38", { "sketchPlane" : qUnion([Q0])});
            skCircle(sketch, "E70", {"center": v(0, -10) * mm, "radius": 1.6 * mm});
            skCircle(sketch, "E71", {"center": v(0, -15) * mm, "radius": 1.6 * mm});
            skLineSegment(sketch, "E72", {"start": v(0, 11.79) * mm, "end": v(0, -11.32) * mm, "construction": true});
            skSolve(sketch);
        }
        {
            var Q0;
            Q0=makeQuery(id+"F38.imprint","IMPRINT",FACE,{"disambiguationData":[TD([[makeQuery(id+"F38.imprint","IMPRINT",EDGE,{"derivedFrom":sQuery(id+"F38.wireOp",EDGE,"E70")}),1.0]])]});
            var Q1;
            Q1=makeQuery(id+"F38.imprint","IMPRINT",FACE,{"disambiguationData":[TD([[makeQuery(id+"F38.imprint","IMPRINT",EDGE,{"derivedFrom":sQuery(id+"F38.wireOp",EDGE,"E71")}),1.0]])]});
            var Q2;
            Q2=sQuery(id+"F38.wireOp",EDGE,"E70");
            var Q3;
            Q3=sQuery(id+"F38.wireOp",EDGE,"E71");
            extrude(context, id + "F39", {"entities" : qUnion([Q0, Q1]), "operationType" : NewBodyOperationType.REMOVE, "surfaceEntities" : qUnion([Q2, Q3]), "oppositeDirection" : true, "depth" : 2 * mm});
        }
        {
            var Q0;
            Q0=makeQuery(id+"F1.opExtrude","SWEPT_FACE",FACE,{"disambiguationData":[OSD([sQuery(id+"F0.wireOp",EDGE,"E0")])]});
            var sketch = newSketch(context, id + "F40", { "sketchPlane" : qUnion([Q0])});
            skCircle(sketch, "E73", {"center": v(0, 7.5) * mm, "radius": 1.6 * mm});
            skCircle(sketch, "E74", {"center": v(0, -7.5) * mm, "radius": 1.6 * mm});
            skLineSegment(sketch, "E75", {"start": v(0, 12.5) * mm, "end": v(0, -12.5) * mm, "construction": true});
            skSolve(sketch);
        }
        {
            var Q0;
            Q0=makeQuery(id+"F40.imprint","IMPRINT",FACE,{"disambiguationData":[TD([[makeQuery(id+"F40.imprint","IMPRINT",EDGE,{"derivedFrom":sQuery(id+"F40.wireOp",EDGE,"E73")}),1.0]])]});
            var Q1;
            Q1=makeQuery(id+"F40.imprint","IMPRINT",FACE,{"disambiguationData":[TD([[makeQuery(id+"F40.imprint","IMPRINT",EDGE,{"derivedFrom":sQuery(id+"F40.wireOp",EDGE,"E74")}),1.0]])]});
            extrude(context, id + "F41", {"entities" : qUnion([Q0, Q1]), "operationType" : NewBodyOperationType.REMOVE, "oppositeDirection" : true, "depth" : 3 * mm});
        }
    });
